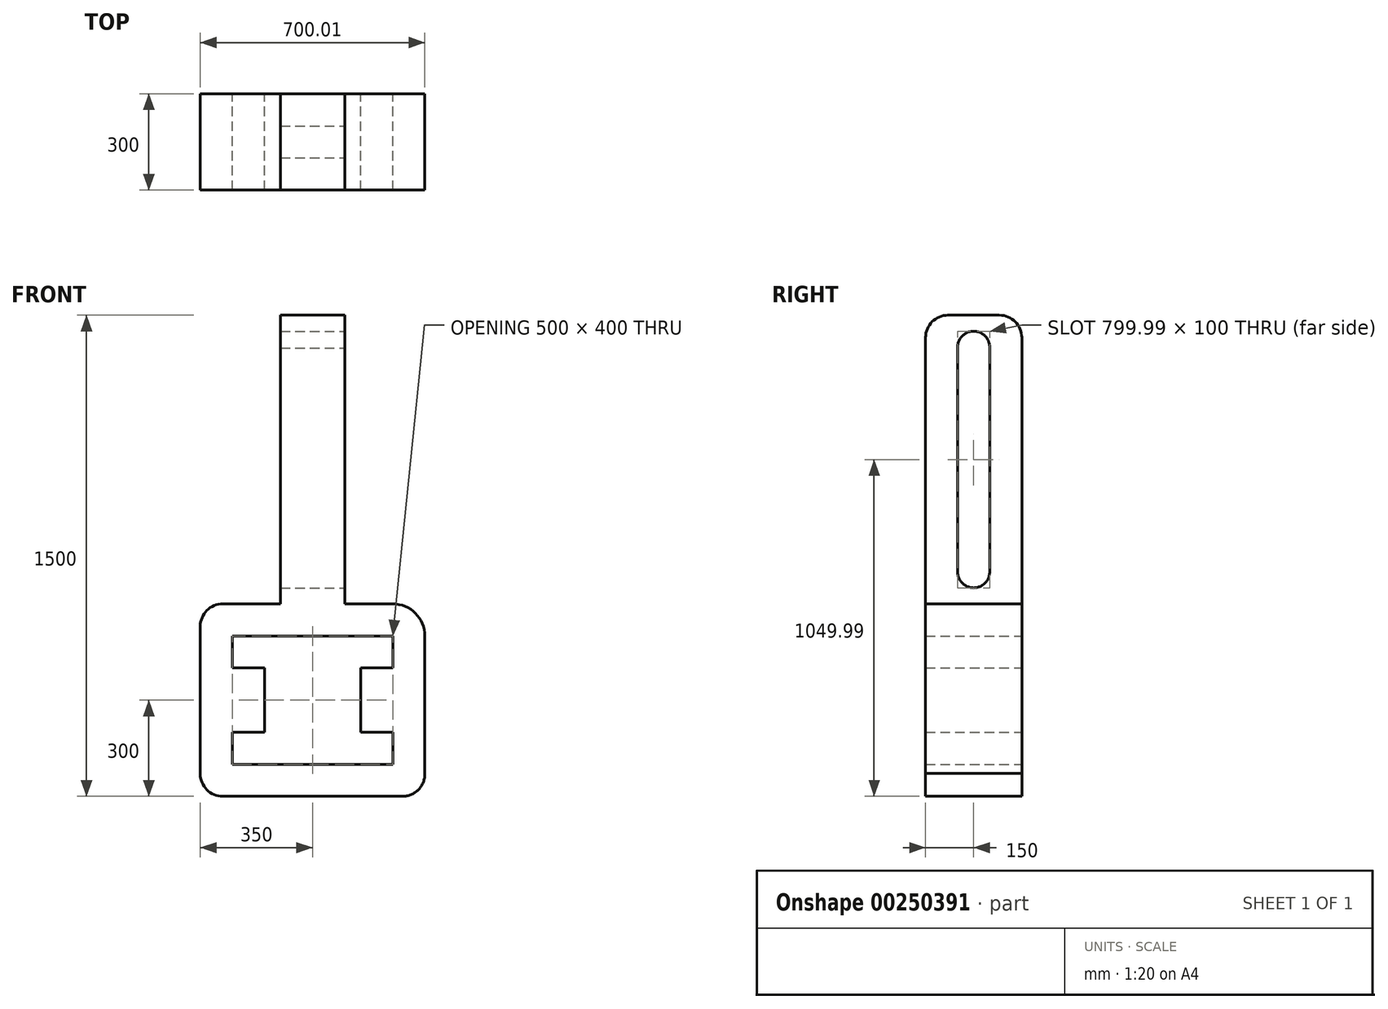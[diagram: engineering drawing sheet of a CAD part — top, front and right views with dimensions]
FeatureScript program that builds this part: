
annotation { "Feature Type Name" : "Feature", "Feature Type Description" : "" }
export const myFeature = defineFeature(function(context is Context, id is Id, definition is map)
    precondition{}
    {
        {
            var Q0;
            Q0=qCreatedBy(makeId("Front.planeOp"),FACE);
            var sketch = newSketch(context, id + "F0", { "sketchPlane" : qUnion([Q0])});
            skLineSegment(sketch, "E0.bottom", {"start": v(280, -300) * mm, "end": v(-280, -300) * mm});
            skLineSegment(sketch, "E0.top", {"start": v(250, 300) * mm, "end": v(100, 300) * mm});
            skLineSegment(sketch, "E0.left", {"start": v(349.98, -227.87) * mm, "end": v(350, 200) * mm});
            skLineSegment(sketch, "E0.right", {"start": v(-350, -230) * mm, "end": v(-350, 230) * mm});
            skPoint(sketch, "E0.middle", {"position": v(0, 0) * mm});
            skArc(sketch, "E1.filletArc", {"start": v(-280, 300) * mm, "mid": v(-329.5, 279.5) * mm, "end": v(-350, 230) * mm});
            skPoint(sketch, "E2.visualSharp", {"position": v(350, 300) * mm});
            skArc(sketch, "E2.filletArc", {"start": v(350, 200) * mm, "mid": v(320.71, 270.71) * mm, "end": v(250, 300) * mm});
            skPoint(sketch, "E3.visualSharp", {"position": v(-350, -300) * mm});
            skArc(sketch, "E3.filletArc", {"start": v(-350, -230) * mm, "mid": v(-329.5, -279.5) * mm, "end": v(-280, -300) * mm});
            skArc(sketch, "E4.filletArc", {"start": v(280, -300) * mm, "mid": v(330.25, -278.74) * mm, "end": v(349.98, -227.87) * mm});
            skLineSegment(sketch, "E5", {"start": v(-250, 200) * mm, "end": v(-250, 100) * mm});
            skLineSegment(sketch, "E6", {"start": v(250, 200) * mm, "end": v(250, 100) * mm});
            skLineSegment(sketch, "E7", {"start": v(-250, 100) * mm, "end": v(-150, 100) * mm});
            skLineSegment(sketch, "E8", {"start": v(250, 100) * mm, "end": v(150, 100) * mm});
            skLineSegment(sketch, "E9", {"start": v(-150, 100) * mm, "end": v(-150, -100) * mm});
            skLineSegment(sketch, "E10", {"start": v(150, 100) * mm, "end": v(150, -100) * mm});
            skLineSegment(sketch, "E11", {"start": v(-150, -100) * mm, "end": v(-250, -100) * mm});
            skLineSegment(sketch, "E12", {"start": v(-250, -100) * mm, "end": v(-250, -200) * mm});
            skLineSegment(sketch, "E13", {"start": v(-250, 200) * mm, "end": v(250, 200) * mm});
            skLineSegment(sketch, "E14", {"start": v(-250, -200) * mm, "end": v(250, -200) * mm});
            skLineSegment(sketch, "E15", {"start": v(250, -200) * mm, "end": v(250, -100) * mm});
            skLineSegment(sketch, "E16", {"start": v(250, -100) * mm, "end": v(150, -100) * mm});
            skLineSegment(sketch, "E17", {"start": v(100, 300) * mm, "end": v(100, 1200) * mm});
            skLineSegment(sketch, "E18", {"start": v(-100, 300) * mm, "end": v(-100, 1200) * mm});
            skLineSegment(sketch, "E19", {"start": v(-100, 1200) * mm, "end": v(100, 1200) * mm});
            skPoint(sketch, "E20.end.orphan", {"position": v(350, 200) * mm});
            skLineSegment(sketch, "E21.trimOffspring", {"start": v(-100, 300) * mm, "end": v(-280, 300) * mm});
            skSolve(sketch);
        }
        {
            var Q0;
            Q0=makeQuery(id+"F0.imprint","IMPRINT",FACE,{"disambiguationData":[TD([[makeQuery(id+"F0.imprint","IMPRINT",EDGE,{"derivedFrom":sQuery(id+"F0.wireOp",EDGE,"E0.bottom")}),-1.0]])]});
            extrude(context, id + "F1", {"entities" : qUnion([Q0]), "depth" : 300 * mm});
        }
        {
            var Q0;
            Q0=makeQuery(id+"F1.opExtrude","CAP_EDGE",EDGE,{"disambiguationData":[OSD([sQuery(id+"F0.wireOp",EDGE,"E19")])],"isStart":true});
            var Q1;
            Q1=makeQuery(id+"F1.opExtrude","CAP_EDGE",EDGE,{"disambiguationData":[OSD([sQuery(id+"F0.wireOp",EDGE,"E19")])],"isStart":false});
            fillet(context, id + "F2", {"entities" : qUnion([Q0, Q1]), "radius" : 70 * mm, "tangentPropagation" : true, "allowEdgeOverflow" : false});
        }
        {
            var Q0;
            Q0=makeQuery(id+"F1.opExtrude","SWEPT_FACE",FACE,{"disambiguationData":[OSD([sQuery(id+"F0.wireOp",EDGE,"E17")])]});
            var sketch = newSketch(context, id + "F3", { "sketchPlane" : qUnion([Q0])});
            skArc(sketch, "E22", {"start": v(-100.07, 1097.33) * mm, "mid": v(-148.88, 1149.99) * mm, "end": v(-200, 1099.56) * mm});
            skArc(sketch, "E23", {"start": v(-200, 400) * mm, "mid": v(-150, 350) * mm, "end": v(-100, 400) * mm});
            skLineSegment(sketch, "E24", {"start": v(-200, 1099.56) * mm, "end": v(-200, 400) * mm});
            skLineSegment(sketch, "E25", {"start": v(-100.07, 1097.33) * mm, "end": v(-100, 400) * mm});
            skSolve(sketch);
        }
        {
            var Q0;
            Q0=makeQuery(id+"F3.imprint","IMPRINT",FACE,{"disambiguationData":[TD([[makeQuery(id+"F3.imprint","IMPRINT",EDGE,{"derivedFrom":sQuery(id+"F3.wireOp",EDGE,"E22")}),1.0]])]});
            extrude(context, id + "F4", {"entities" : qUnion([Q0]), "oppositeDirection" : true, "depth" : 1454 * mm});
        }
        {
            var Q0;
            Q0=makeQuery(id+"F4.opExtrude","SWEPT_BODY",BODY,{"disambiguationData":[OSD([sQuery(id+"F3.wireOp",EDGE,"E22"),sQuery(id+"F3.wireOp",EDGE,"E23"),sQuery(id+"F3.wireOp",EDGE,"E24"),sQuery(id+"F3.wireOp",EDGE,"E25")])]});
            var Q1;
            Q1=makeQuery(id+"F1.opExtrude","SWEPT_BODY",BODY,{"disambiguationData":[OSD([sQuery(id+"F0.wireOp",EDGE,"E0.bottom"),sQuery(id+"F0.wireOp",EDGE,"E0.top"),sQuery(id+"F0.wireOp",EDGE,"E0.left"),sQuery(id+"F0.wireOp",EDGE,"E0.right"),sQuery(id+"F0.wireOp",EDGE,"E1.filletArc"),sQuery(id+"F0.wireOp",EDGE,"E2.filletArc"),sQuery(id+"F0.wireOp",EDGE,"E3.filletArc"),sQuery(id+"F0.wireOp",EDGE,"E4.filletArc"),sQuery(id+"F0.wireOp",EDGE,"E5"),sQuery(id+"F0.wireOp",EDGE,"E6"),sQuery(id+"F0.wireOp",EDGE,"E7"),sQuery(id+"F0.wireOp",EDGE,"E8"),sQuery(id+"F0.wireOp",EDGE,"E9"),sQuery(id+"F0.wireOp",EDGE,"E10"),sQuery(id+"F0.wireOp",EDGE,"E11"),sQuery(id+"F0.wireOp",EDGE,"E12"),sQuery(id+"F0.wireOp",EDGE,"E13"),sQuery(id+"F0.wireOp",EDGE,"E14"),sQuery(id+"F0.wireOp",EDGE,"E15"),sQuery(id+"F0.wireOp",EDGE,"E16"),sQuery(id+"F0.wireOp",EDGE,"E17"),sQuery(id+"F0.wireOp",EDGE,"E18"),sQuery(id+"F0.wireOp",EDGE,"E19"),sQuery(id+"F0.wireOp",EDGE,"E21.trimOffspring")])]});
            booleanBodies(context, id + "F5", {"operationType" : BooleanOperationType.SUBTRACTION, "tools" : qUnion([Q0]), "targets" : qUnion([Q1])});
        }
    });
